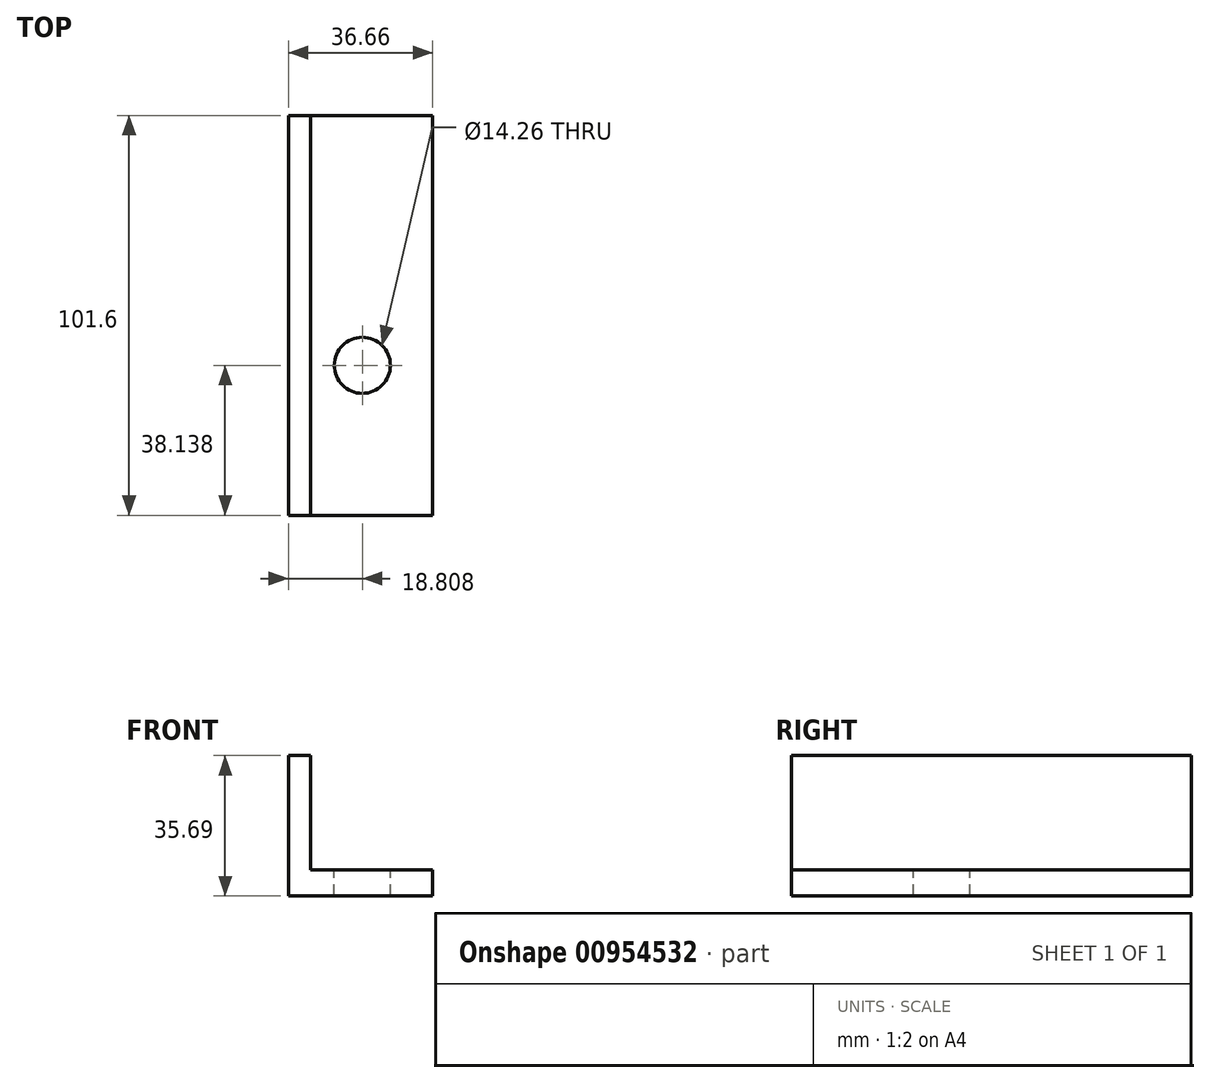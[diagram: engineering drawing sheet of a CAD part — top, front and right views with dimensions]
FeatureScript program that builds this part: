
annotation { "Feature Type Name" : "Feature", "Feature Type Description" : "" }
export const myFeature = defineFeature(function(context is Context, id is Id, definition is map)
    precondition{}
    {
        {
            var Q0;
            Q0=qCreatedBy(makeId("Front.planeOp"),FACE);
            var sketch = newSketch(context, id + "F0", { "sketchPlane" : qUnion([Q0])});
            skLineSegment(sketch, "E0", {"start": v(0, 0) * mm, "end": v(36.66, 0) * mm});
            skLineSegment(sketch, "E1", {"start": v(36.66, 0) * mm, "end": v(36.66, 6.58) * mm});
            skLineSegment(sketch, "E2", {"start": v(36.66, 6.58) * mm, "end": v(5.6, 6.58) * mm});
            skLineSegment(sketch, "E3", {"start": v(5.6, 6.58) * mm, "end": v(5.6, 35.7) * mm});
            skLineSegment(sketch, "E4", {"start": v(5.6, 35.7) * mm, "end": v(0, 35.7) * mm});
            skLineSegment(sketch, "E5", {"start": v(0, 35.7) * mm, "end": v(0, 0) * mm});
            skSolve(sketch);
        }
        {
            var Q0;
            Q0 = qSketchRegion(id + "F0", true);
            extrude(context, id + "F1", {"entities" : qUnion([Q0]), "depth" : 101.6 * mm, "offsetDistance" : 25.4 * mm, "symmetric" : true});
        }
        {
            var Q0;
            Q0=makeQuery(id+"F1.opExtrude","SWEPT_FACE",FACE,{"disambiguationData":[OSD([sQuery(id+"F0.wireOp",EDGE,"E2")])]});
            var sketch = newSketch(context, id + "F2", { "sketchPlane" : qUnion([Q0])});
            skCircle(sketch, "E6", {"center": v(18.8, -12.66) * mm, "radius": 7.13 * mm});
            skSolve(sketch);
        }
        {
            var Q0;
            Q0 = qSketchRegion(id + "F2", true);
            extrude(context, id + "F3", {"entities" : qUnion([Q0]), "operationType" : NewBodyOperationType.REMOVE, "oppositeDirection" : true, "depth" : 25.4 * mm, "offsetDistance" : 25.4 * mm});
        }
    });
